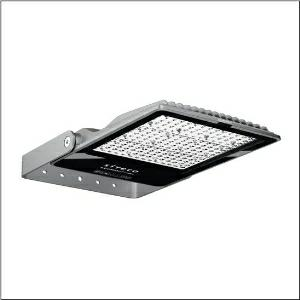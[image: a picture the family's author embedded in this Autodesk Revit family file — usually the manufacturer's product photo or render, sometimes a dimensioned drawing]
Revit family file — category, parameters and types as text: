
# Revit family: sicompact_r__31_midi___pl32_5xa7581d1k23_6975
name_source: partatom
category: Lighting Fixtures
units: mm (PartAtom-declared; Revit-internal decimal feet)

## family parameters
Cut with Voids When Loaded = No
Host = Face
Light Source = No
Part Type = Normal
Room Calculation Point = No
Round Connector Dimension = Use Diameter
Shared = No

## types (1)
- SiCompact® 31 midi  PL32 (1 x LED, 27000 lm, 171 W, 3000K)
    Apparent Load = 171 VA
    CIE Flux Codes = 32 69 98 100 100
    Color Rendering = 70
    Color Temperature = 3000K
    Default Elevation = 1800 mm
    Description = SiCompact® 31 midi, floodlight, primary light control with lens, of plastic, of toughened safety glass, transparent, light distribution: PL32, light emission: direct distribution, primary light characteristic: asymmetric, installation type: surface-mounted, LED, High Power LED, rated luminous flux: 27.000lm, luminous efficacy: 158lm/W, light colour: 730, colour temperature: 3000K, control gear: ECG, with cable, 3x 1.5mm², mains connection: 220..240V, AC, 50/60Hz, connection cable pre-assembled, cable length: 2m, rated input power: 171W, of diecast aluminium, specular, metallic grey (RAL 9006), length: 560mm, width: 330mm, height: 62mm, bracket, of sheet steel, coated, metallic grey (RAL 9006), ON/OFF, protection rating (complete): IP66, insulation class (complete): insulation class I (protective earthing), certification: CE, impact resistance: IK08, permissible operating ambient temperature: -40..+45°C, packaging unit: 1 piece

Light Distribution: PL32
    Height = 62 mm  [stored 0.203412 ft]
    Lamp = 1 x LED
    Lamp Light Flux = 27000 lm
    Lamp Power = 171 W
    Lamp count = 1
    Length = 560 mm
    Luminous efficacy = 158 lm/W
    Manufacturer = Siteco
    ModVariant = No
    Model = 5XA7581D1K23
    Number of Poles = 1
    OnlyDefault = Yes
    Power Factor = 1
    Product Name = SiCompact® 31 midi | PL32
    Product group = floodlight | pylon top
    ProductGroupID = 6101
    Protection Class = Protection class I
    Protection Degree = IP 66
    RLX_Detail_Level = 1
    RlxData = <blob elided: 97849 chars, md5=0141fb9b>
    Socket = socket
    Standby Power = 0 W
    System Light Flux = 27000 lm
    System Power = 171 W
    Type Comments = Product without accessories
    Type Image = l_1006415.jpg
    URL = http://relux.com
    VarID = ---
    Voltage = 0 V
    Weight = 0.00 kg
    Width = 333 mm

note: [stored X ft] marks values corroborated as IEEE doubles in the binary element streams (Revit-internal decimal feet)

## geometry (parser evidence)
native form markers: Blend x4, Sweep x12
no freeform markers — native parametric forms only
